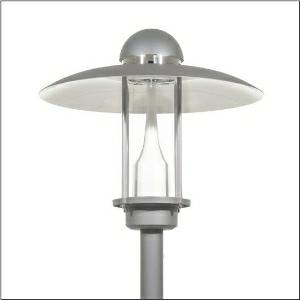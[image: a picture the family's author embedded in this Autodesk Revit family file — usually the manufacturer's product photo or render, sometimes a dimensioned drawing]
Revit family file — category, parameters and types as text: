
# Revit family: city-light_elegance_iq___p1_0a_5xa5265bf14h_371a
name_source: partatom
category: Lighting Fixtures
units: mm (PartAtom-declared; Revit-internal decimal feet)

## family parameters
Cut with Voids When Loaded = No
Host = Face
Light Source = No
Part Type = Normal
Room Calculation Point = No
Round Connector Dimension = Use Diameter
Shared = No

## types (1)
- --- (1 x LED, 1440 lm, 12.9 W, 2200K)
    Apparent Load = 13 VA
    CIE Flux Codes = 32 62 91 97 100
    Color Rendering = 70
    Color Temperature = 2200K
    Default Elevation = 1800 mm
    Description = City-Light Elegance iQ, mast luminaire, Module 540 iQ-SR, primary light control with 3 zone facetted reflector, of plastic, silver coated, highly specular, structured, primary optical cover: cover, of PMMA, transparent, light distribution: P1.0a, light emission: direct distribution, primary light characteristic: strongly asymmetric, installation type: post-top, LED, High Power LED, rated luminous flux: 1.440lm, luminous efficacy: 112lm/W, light colour: 722, colour temperature: 2200K, control gear: iQ Street-Remote, control: pre-setting: logarithmic dimming characteristic, Street-Remote, Auto-Match, Temp-Guard, Lumen-Switch, Night-Set, Smart-Wire, Light-Fading, Desk-Remote (wireless, voltage-free reading and setting of iQ features in the workshop via application-optimized NFC function/RFID function), optimised constant luminous flux control (CLO 2.0), with terminal, 6-pole, max. 2.5mm², mains connection: 230..240V, AC, 50/60Hz, start of lifetime: 13W, end of service life: 13W, reduction: 6W, luminaire housing, upper part, of aluminium, coated, Siteco® metallic grey (DB 702S), diameter: 750mm, height: 675mm, spigot size: d x l = 76 x 70mm (post-top) | with reducer (optional accessory) 60 x 70mm, mounting height: 3..5m, post-top mast mounting element, of diecast aluminium, coated, Siteco® metallic grey (DB 702S), Module 540 iQ-SR, traffic white (RAL 9016), equipment: standard, protection rating (complete): IP65, insulation class (complete): insulation class II (safety insulation), certification: CE, ENEC, VDE, packaging unit: 1 piece

Light Distribution: P1.0a
    Height = 675 mm
    Lamp = 1 x LED
    Lamp Light Flux = 1440 lm
    Lamp Power = 12.9 W
    Lamp count = 1
    Length = 750 mm
    Luminous efficacy = 112 lm/W
    Manufacturer = Siteco
    ModVariant = No
    Model = 5XA5265BF14H
    Number of Poles = 1
    OnlyDefault = Yes
    Power Factor = 1
    Product Name = City-Light Elegance iQ | P1.0a
    Product group = mast luminaire | pylon top
    ProductGroupID = 6100
    Protection Class = Protection class II
    Protection Degree = IP 65
    RLX_Detail_Level = 1
    RLX_Emergency_Light_Flux = 0 lm
    RLX_Emergency_Type = 0
    RLX_Emergency_Type_DB = No
    RlxData = <blob elided: 63313 chars, md5=94b11d5a>
    Socket = socket
    Standby Power = 0 W
    System Light Flux = 1440 lm
    System Power = 13 W
    Type Comments = factory setting: luminous flux: 100 % | dim-lin: 254 | 516 mA
    Type Image = l_1006912.jpg
    URL = http://relux.com
    VarID = @adj_159782
    Voltage = 0 V
    Weight = 0.00 kg
    Width = 0 mm  [stored 0 ft]

note: [stored X ft] marks values corroborated as IEEE doubles in the binary element streams (Revit-internal decimal feet)

## geometry (parser evidence)
native form markers: Blend x4, Sweep x12
no freeform markers — native parametric forms only
